# Revit family: Toilet-Floor_Mount-KOHLER-San_Souci-K-4007_1
name_source: partatom
category: Plumbing Fixtures
units: mm (PartAtom-declared; Revit-internal decimal feet)

## family parameters
Cut with Voids When Loaded = No
Host = Face
OmniClass Number = 23.31.19.00
OmniClass Title = Toilets
Part Type = Normal
Room Calculation Point = No
Round Connector Dimension = Use Diameter
Shared = No

## types (10) — shared parameters
ADA Compliant = No
Assembly Code = D2010100
Bowl Height = 15 3/16"
CW Connection = Yes
Cold Water Inlet = Cold Water Inlet
Date Modified = 08/05/2024
Default Elevation = 0"
Description = One-Piece Round-Front Toilet, 1.28 GPF
Flow Rate = 0 GPM
Flush Rate = 1.28 GPF
HW Connection = No
Height = 24"
Hot Water Inlet = Hot Water Inlet
Length = 25 1/2"
Manufacturer = Kohler Co.
MasterFormat 1995 = 15410
MasterFormat 2004 = 22.41.13
Material = Vitreous china
Pressure = 80.00 psi
Product Documentation Link = https://www.us.kohler.com
Product Name = San Souci
Product Page URL = http://www.us.kohler.com
Rough-In = 12"
Seat Included = Yes
URL = https://www.us.kohler.com
Vent Connection = No
Waste Connection = Yes
Waste Water Outlet = Waste Water Outlet
WaterSense Certified = Yes
Width = 16 3/4"

## per-type parameters (varying)
| type | 26802_Seat | 27332_Seat | Finish | Model | Type |
| 0-White | No | Yes | Kohler-Vitreous_China-0-White | K-4007-0 | 1 |
| 96-Biscuit | No | Yes | Kohler-Vitreous_China-96-Biscuit | K-4007-96 | 2 |
| 47-Almond | No | Yes | Kohler-Vitreous_China-47-Almond | K-4007-47 | 3 |
| NY-Dune | Yes | No | Kohler-Vitreous_China-NY-Dune | K-4007-NY | 4 |
| 95-Ice Grey | Yes | No | Kohler-Vitreous_China-95-Ice_Grey | K-4007-95 | 5 |
| G9-Sandbar | No | Yes | Kohler-Vitreous_China-G9-Sandbar | K-4007-G9 | 6 |
| 33-Mexican Sand | No | Yes | Kohler-Vitreous_China-33-Mexican_Sand | K-4007-33 | 7 |
| K4-Cashmere | No | Yes | Kohler-Vitreous_China-K4-Cashmere | K-4007-K4 | 8 |
| 58-Thunder Grey | Yes | No | Kohler-Vitreous_China-58-Thunder_Grey | K-4007-58 | 9 |
| 7-Black Black | Yes | No | Kohler-Vitreous_China-7-Black_Black | K-4007-7 | 10 |

## geometry (parser evidence)
native form markers: Sweep x8
no freeform markers — native parametric forms only
